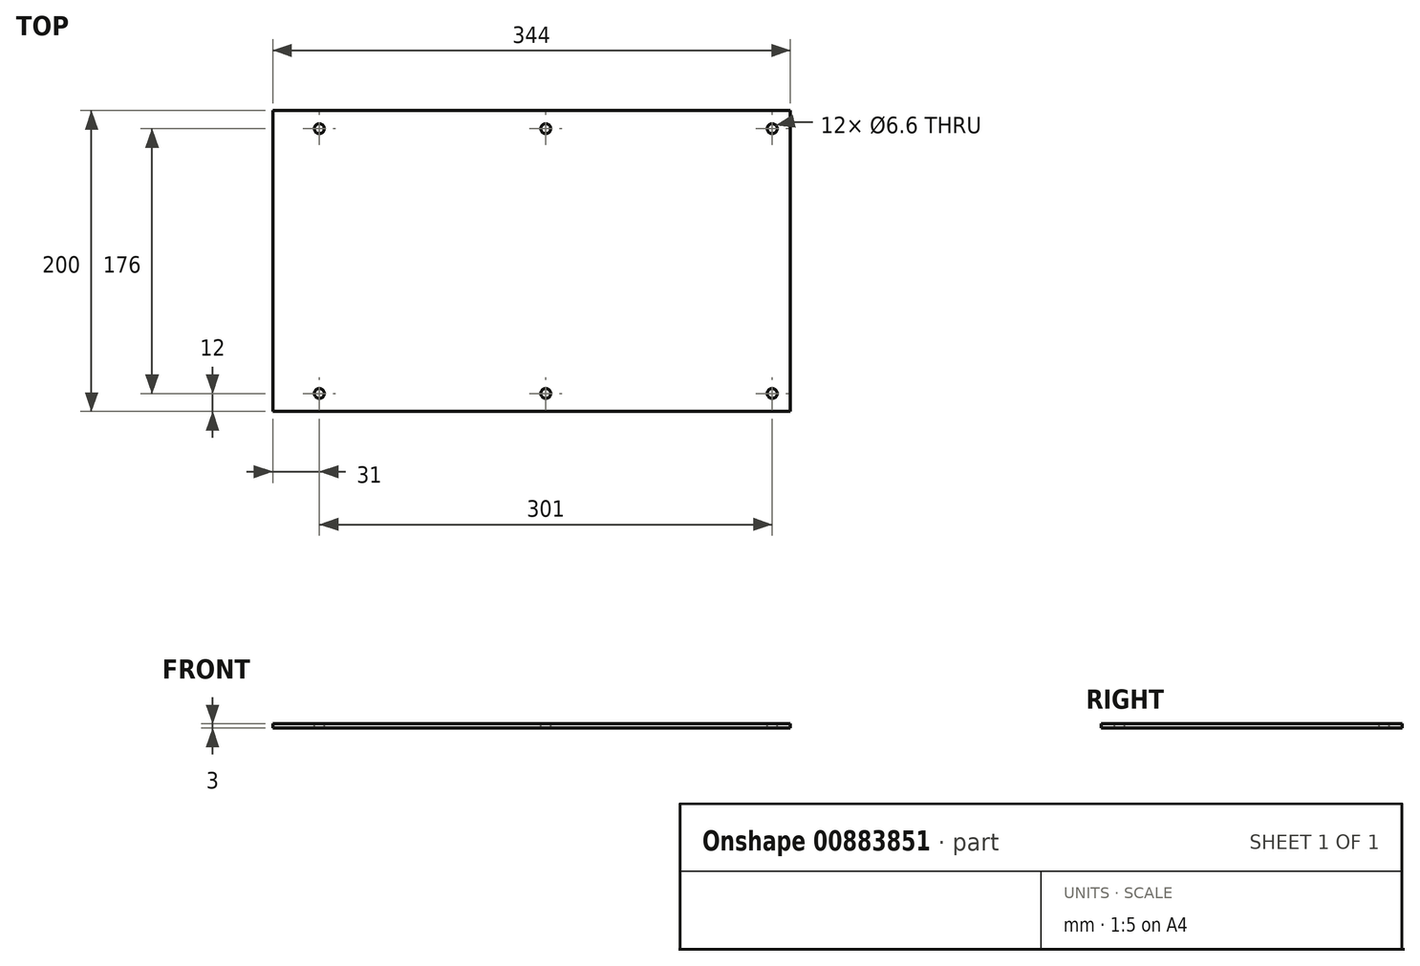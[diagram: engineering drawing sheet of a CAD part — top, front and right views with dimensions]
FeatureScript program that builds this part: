
annotation { "Feature Type Name" : "Feature", "Feature Type Description" : "" }
export const myFeature = defineFeature(function(context is Context, id is Id, definition is map)
    precondition{}
    {
        {
            var Q0;
            Q0=qCreatedBy(makeId("Top.planeOp"),FACE);
            var sketch = newSketch(context, id + "F0", { "sketchPlane" : qUnion([Q0])});
            skLineSegment(sketch, "E0.bottom", {"start": v(0, 0) * mm, "end": v(344, 0) * mm});
            skLineSegment(sketch, "E0.top", {"start": v(0, 200) * mm, "end": v(344, 200) * mm});
            skLineSegment(sketch, "E0.left", {"start": v(0, 0) * mm, "end": v(0, 200) * mm});
            skLineSegment(sketch, "E0.right", {"start": v(344, 0) * mm, "end": v(344, 200) * mm});
            skSolve(sketch);
        }
        {
            var Q0;
            Q0 = qSketchRegion(id + "F0", true);
            extrude(context, id + "F1", {"entities" : qUnion([Q0]), "depth" : 3 * mm, "offsetDistance" : 25 * mm});
        }
        {
            var Q0;
            Q0=makeQuery(id+"F1.opExtrude","CAP_FACE",FACE,{"disambiguationData":[OSD([sQuery(id+"F0.wireOp",EDGE,"E0.bottom"),sQuery(id+"F0.wireOp",EDGE,"E0.top"),sQuery(id+"F0.wireOp",EDGE,"E0.left"),sQuery(id+"F0.wireOp",EDGE,"E0.right")])],"isStart":false});
            var sketch = newSketch(context, id + "F2", { "sketchPlane" : qUnion([Q0])});
            skCircle(sketch, "E1", {"center": v(31, 12) * mm, "radius": 3.3 * mm});
            skCircle(sketch, "E2", {"center": v(181.5, 12) * mm, "radius": 3.3 * mm});
            skCircle(sketch, "E3", {"center": v(332, 12) * mm, "radius": 3.3 * mm});
            skSolve(sketch);
        }
        {
            var Q0;
            Q0 = qSketchRegion(id + "F2", true);
            extrude(context, id + "F3", {"entities" : qUnion([Q0]), "operationType" : NewBodyOperationType.REMOVE, "oppositeDirection" : true, "depth" : 25 * mm, "offsetDistance" : 25 * mm});
        }
        {
            var Q0;
            Q0=makeQuery(id+"F1.opExtrude","CAP_FACE",FACE,{"disambiguationData":[OSD([sQuery(id+"F0.wireOp",EDGE,"E0.bottom"),sQuery(id+"F0.wireOp",EDGE,"E0.top"),sQuery(id+"F0.wireOp",EDGE,"E0.left"),sQuery(id+"F0.wireOp",EDGE,"E0.right")])],"isStart":false});
            var sketch = newSketch(context, id + "F4", { "sketchPlane" : qUnion([Q0])});
            skCircle(sketch, "E4", {"center": v(31, 188) * mm, "radius": 3.3 * mm});
            skCircle(sketch, "E5", {"center": v(181.5, 188) * mm, "radius": 3.3 * mm});
            skCircle(sketch, "E6", {"center": v(332, 188) * mm, "radius": 3.3 * mm});
            skSolve(sketch);
        }
        {
            var Q0;
            Q0 = qSketchRegion(id + "F4", true);
            extrude(context, id + "F5", {"entities" : qUnion([Q0]), "operationType" : NewBodyOperationType.REMOVE, "oppositeDirection" : true, "depth" : 25 * mm, "offsetDistance" : 25 * mm});
        }
        {
            var Q0;
            Q0=makeQuery(id+"F1.opExtrude","SWEPT_BODY",BODY,{"disambiguationData":[OSD([sQuery(id+"F0.wireOp",EDGE,"E0.bottom"),sQuery(id+"F0.wireOp",EDGE,"E0.top"),sQuery(id+"F0.wireOp",EDGE,"E0.left"),sQuery(id+"F0.wireOp",EDGE,"E0.right")])]});
            transform(context, id + "F6", {"entities" : qUnion([Q0]), "transformType" : TransformType.TRANSLATION_3D, "dx" : 0 * mm, "dy" : 0 * mm, "dz" : 0 * mm, "makeCopy" : true});
        }
    });
